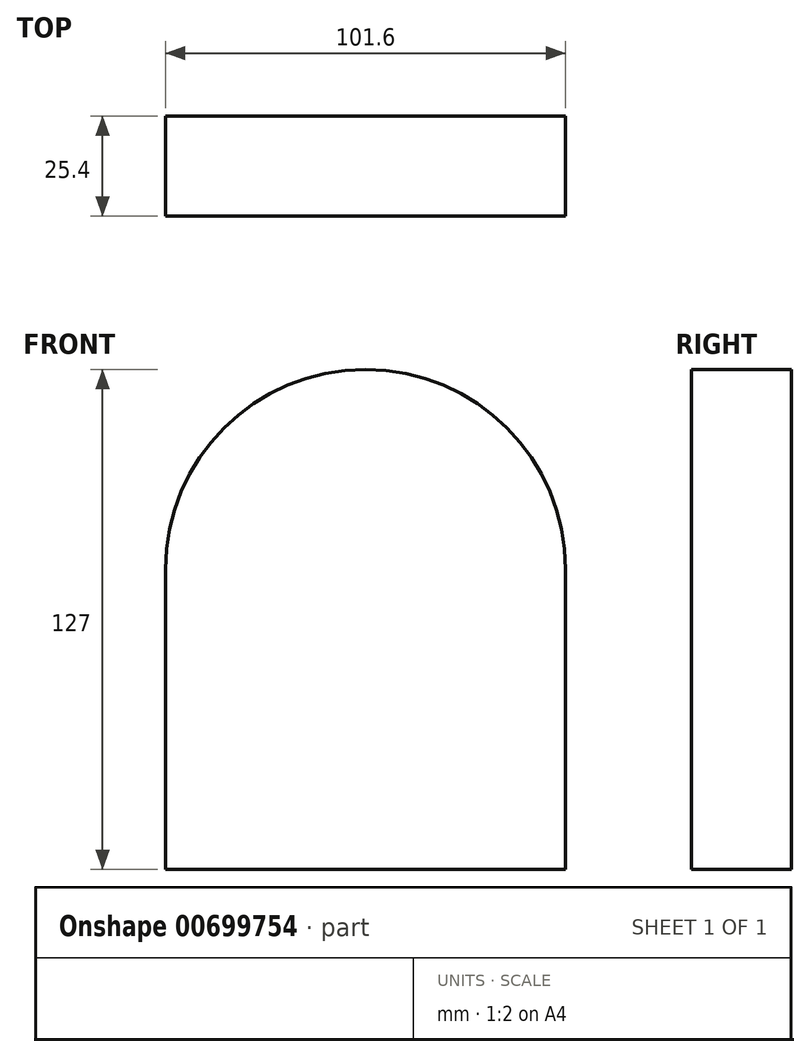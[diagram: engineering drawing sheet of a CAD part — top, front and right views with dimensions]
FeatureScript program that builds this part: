
annotation { "Feature Type Name" : "Feature", "Feature Type Description" : "" }
export const myFeature = defineFeature(function(context is Context, id is Id, definition is map)
    precondition{}
    {
        {
            var Q0;
            Q0=qCreatedBy(makeId("Front.planeOp"),FACE);
            var sketch = newSketch(context, id + "F0", { "sketchPlane" : qUnion([Q0])});
            skLineSegment(sketch, "E0", {"start": v(-39.56, -60.18) * mm, "end": v(-39.56, 66.82) * mm});
            skLineSegment(sketch, "E1", {"start": v(-39.56, 66.82) * mm, "end": v(62.04, 66.82) * mm});
            skLineSegment(sketch, "E2", {"start": v(62.04, 66.82) * mm, "end": v(62.04, -60.18) * mm});
            skLineSegment(sketch, "E3", {"start": v(62.04, -60.18) * mm, "end": v(-39.56, -60.18) * mm});
            skSolve(sketch);
        }
        {
            var Q0;
            Q0 = qSketchRegion(id + "F0", true);
            extrude(context, id + "F1", {"entities" : qUnion([Q0]), "depth" : 25.4 * mm, "offsetDistance" : 25.4 * mm});
        }
        {
            var Q0;
            Q0=makeQuery(id+"F1.opExtrude","SWEPT_EDGE",EDGE,{"disambiguationData":[OSD([sQuery(id+"F0.wireOp",EDGE,"E1"),sQuery(id+"F0.wireOp",EDGE,"E2")])]});
            var Q1;
            Q1=makeQuery(id+"F1.opExtrude","SWEPT_EDGE",EDGE,{"disambiguationData":[OSD([sQuery(id+"F0.wireOp",EDGE,"E0"),sQuery(id+"F0.wireOp",EDGE,"E1")])]});
            fillet(context, id + "F2", {"entities" : qUnion([Q0, Q1]), "radius" : 50.8 * mm, "tangentPropagation" : true, "allowEdgeOverflow" : false});
        }
    });
